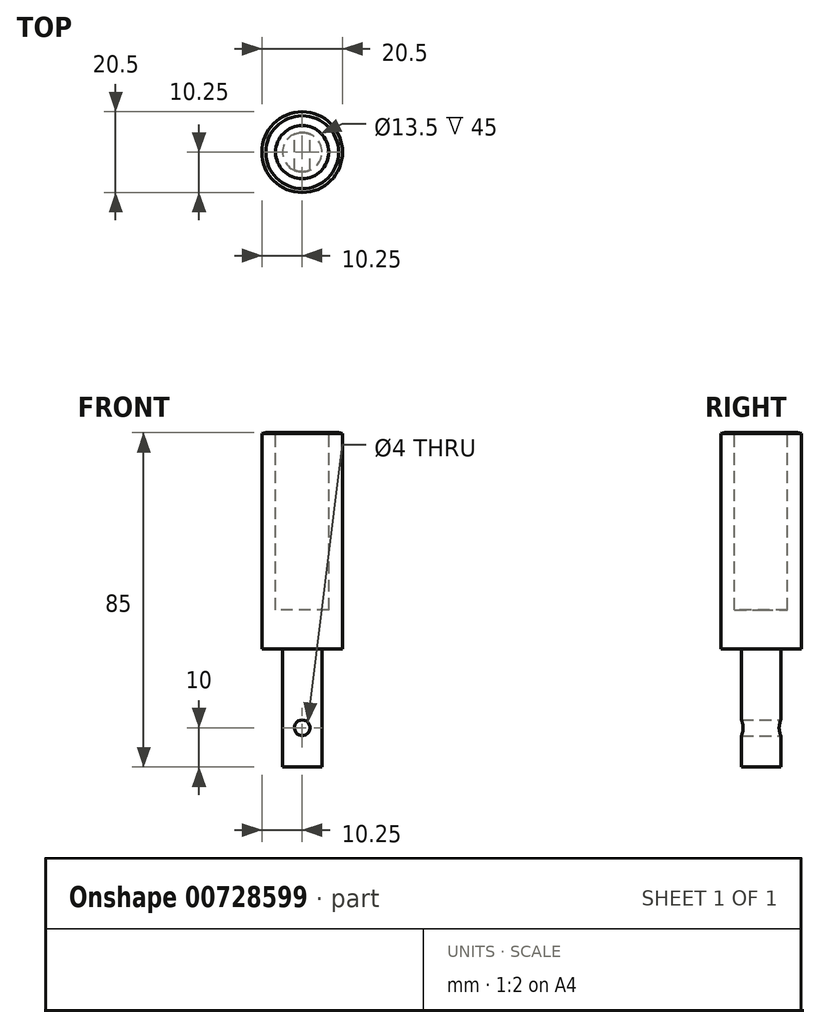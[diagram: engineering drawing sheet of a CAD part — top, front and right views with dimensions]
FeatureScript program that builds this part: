
annotation { "Feature Type Name" : "Feature", "Feature Type Description" : "" }
export const myFeature = defineFeature(function(context is Context, id is Id, definition is map)
    precondition{}
    {
        {
            var Q0;
            Q0=qCreatedBy(makeId("Top.planeOp"),FACE);
            var sketch = newSketch(context, id + "F0", { "sketchPlane" : qUnion([Q0])});
            skCircle(sketch, "E0", {"center": v(0, 0) * mm, "radius": 5 * mm});
            skSolve(sketch);
        }
        {
            var Q0;
            Q0 = qSketchRegion(id + "F0", true);
            extrude(context, id + "F1", {"entities" : qUnion([Q0]), "depth" : 30 * mm, "offsetDistance" : 25 * mm});
        }
        {
            var Q0;
            Q0=makeQuery(id+"F1.opExtrude","CAP_FACE",FACE,{"disambiguationData":[OSD([sQuery(id+"F0.wireOp",EDGE,"E0")])],"isStart":false});
            var sketch = newSketch(context, id + "F2", { "sketchPlane" : qUnion([Q0])});
            skCircle(sketch, "E1", {"center": v(0, 0) * mm, "radius": 10.25 * mm});
            skSolve(sketch);
        }
        {
            var Q0;
            Q0 = qSketchRegion(id + "F2", true);
            extrude(context, id + "F3", {"entities" : qUnion([Q0]), "operationType" : NewBodyOperationType.ADD, "depth" : 55 * mm, "offsetDistance" : 25 * mm});
        }
        {
            var Q0;
            Q0=makeQuery(id+"F3.opExtrude","CAP_FACE",FACE,{"disambiguationData":[OSD([sQuery(id+"F2.wireOp",EDGE,"E1")])],"isStart":false});
            var sketch = newSketch(context, id + "F4", { "sketchPlane" : qUnion([Q0])});
            skCircle(sketch, "E2", {"center": v(0, 0) * mm, "radius": 6.75 * mm});
            skSolve(sketch);
        }
        {
            var Q0;
            Q0 = qSketchRegion(id + "F4", true);
            extrude(context, id + "F5", {"entities" : qUnion([Q0]), "operationType" : NewBodyOperationType.REMOVE, "oppositeDirection" : true, "depth" : 45 * mm, "offsetDistance" : 25 * mm});
        }
        {
            var Q0;
            Q0=makeQuery(id+"F3.opExtrude","CAP_EDGE",EDGE,{"disambiguationData":[OSD([sQuery(id+"F2.wireOp",EDGE,"E1")])],"isStart":false});
            chamfer(context, id + "F6", {"entities" : qUnion([Q0]), "chamferType" : ChamferType.OFFSET_ANGLE, "width" : 1 * mm, "oppositeDirection" : false, "angle" : 15 * degree, "tangentPropagation" : true});
        }
        {
            var Q0;
            Q0=qCreatedBy(makeId("Front.planeOp"),FACE);
            var sketch = newSketch(context, id + "F7", { "sketchPlane" : qUnion([Q0])});
            skCircle(sketch, "E3", {"center": v(0, 10) * mm, "radius": 2 * mm});
            skSolve(sketch);
        }
        {
            var Q0;
            Q0 = qSketchRegion(id + "F7", true);
            extrude(context, id + "F8", {"entities" : qUnion([Q0]), "operationType" : NewBodyOperationType.REMOVE, "endBound" : BoundingType.SYMMETRIC, "depth" : 20 * mm, "offsetDistance" : 25 * mm});
        }
    });
